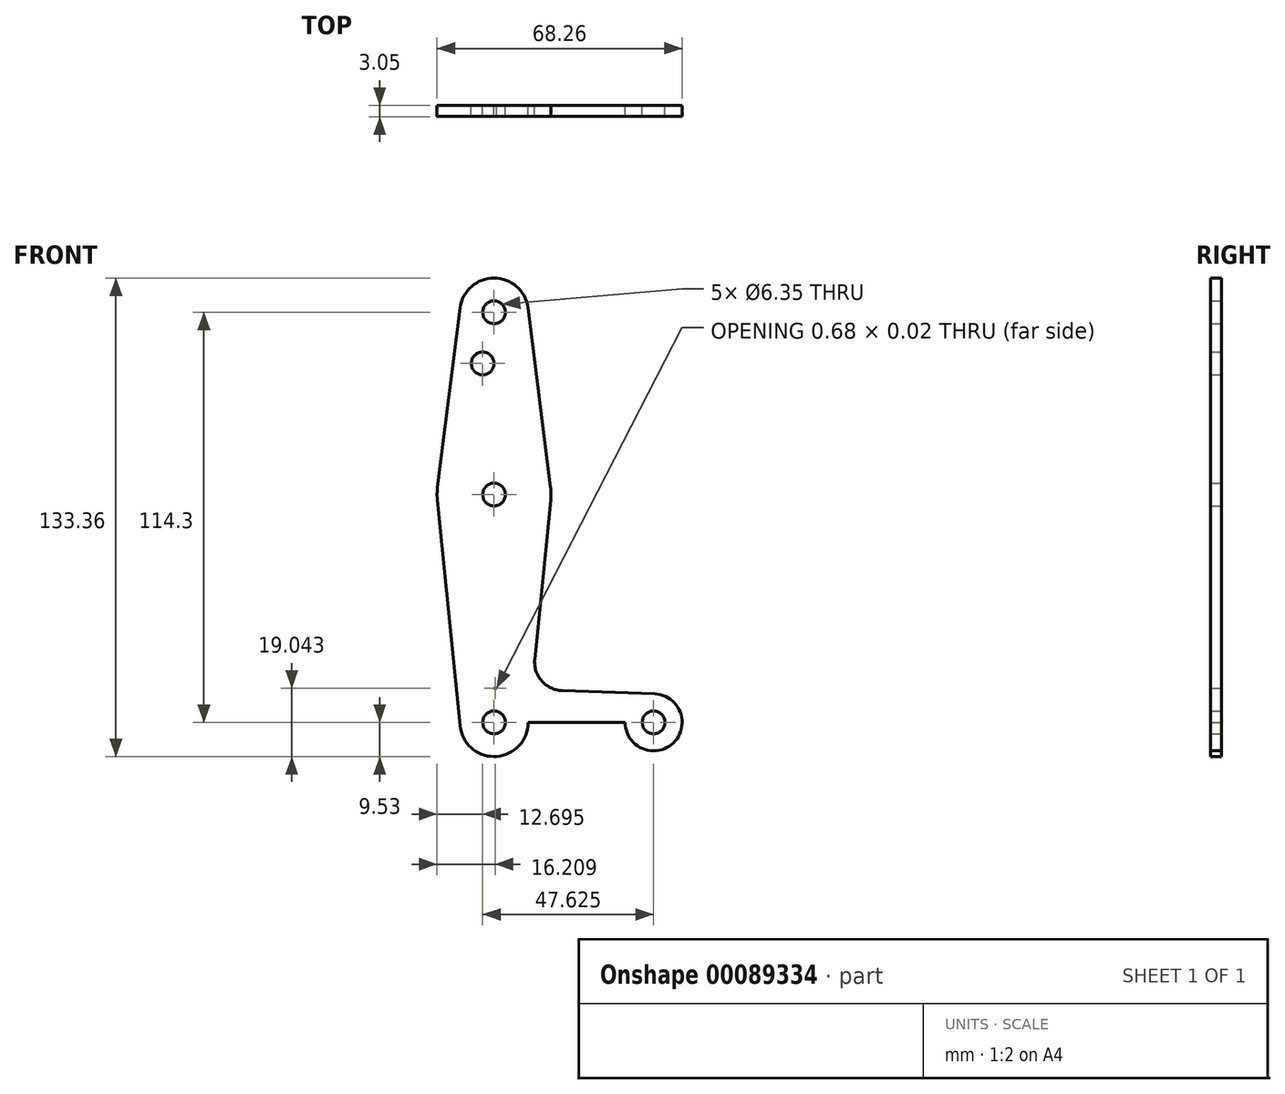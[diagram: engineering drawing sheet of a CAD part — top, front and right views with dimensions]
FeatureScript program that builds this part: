
annotation { "Feature Type Name" : "Feature", "Feature Type Description" : "" }
export const myFeature = defineFeature(function(context is Context, id is Id, definition is map)
    precondition{}
    {
        {
            var Q0;
            Q0=qCreatedBy(makeId("Front.planeOp"),FACE);
            var sketch = newSketch(context, id + "F0", { "sketchPlane" : qUnion([Q0])});
            skCircle(sketch, "E0", {"center": v(0, 114.3) * mm, "radius": 9.53 * mm});
            skCircle(sketch, "E1", {"center": v(0, 63.5) * mm, "radius": 15.88 * mm});
            skCircle(sketch, "E2", {"center": v(0, 0) * mm, "radius": 9.53 * mm});
            skCircle(sketch, "E3", {"center": v(44.45, 0) * mm, "radius": 7.94 * mm});
            skLineSegment(sketch, "E4", {"start": v(0, 114.3) * mm, "end": v(0, 0) * mm});
            skLineSegment(sketch, "E5", {"start": v(0, 0) * mm, "end": v(44.45, 0) * mm});
            skLineSegment(sketch, "E6", {"start": v(-9.45, 115.5) * mm, "end": v(-15.75, 65.48) * mm});
            skLineSegment(sketch, "E7", {"start": v(9.45, 115.5) * mm, "end": v(15.75, 65.48) * mm});
            skLineSegment(sketch, "E8", {"start": v(15.8, 61.91) * mm, "end": v(11.34, 17.59) * mm});
            skLineSegment(sketch, "E9", {"start": v(44.73, 7.93) * mm, "end": v(18.97, 8.85) * mm});
            skPoint(sketch, "E9.endSnap0", {"position": v(0, 57.15) * mm});
            skLineSegment(sketch, "E10", {"start": v(-15.8, 61.91) * mm, "end": v(-9.48, -0.95) * mm});
            skLineSegment(sketch, "E11", {"start": v(0, -9.52) * mm, "end": v(44.73, -7.93) * mm});
            skCircle(sketch, "E12", {"center": v(0, 114.3) * mm, "radius": 3.18 * mm});
            skCircle(sketch, "E13", {"center": v(-3.17, 100.03) * mm, "radius": 3.18 * mm});
            skCircle(sketch, "E14", {"center": v(0, 63.5) * mm, "radius": 3.18 * mm});
            skCircle(sketch, "E15", {"center": v(0, 0) * mm, "radius": 3.18 * mm});
            skCircle(sketch, "E16", {"center": v(44.45, 0) * mm, "radius": 3.18 * mm});
            skArc(sketch, "E17", {"start": v(11.34, 17.59) * mm, "mid": v(13.26, 11.57) * mm, "end": v(18.97, 8.85) * mm});
            skLineSegment(sketch, "E18.trimOffspring", {"start": v(0.68, 9.5) * mm, "end": v(0, 9.52) * mm});
            skSolve(sketch);
        }
        {
            var Q0;
            {var subQ5=sQuery(id+"F0.wireOp",EDGE,"E6");Q0=makeQuery(id+"F0.imprint","IMPRINT",FACE,{"disambiguationData":[TD([[makeQuery(id+"F0.imprint","IMPRINT",EDGE,{"derivedFrom":subQ5}),1.0]])]});}
            var Q1;
            {var subQ6=sQuery(id+"F0.wireOp",EDGE,"E7");Q1=makeQuery(id+"F0.imprint","IMPRINT",FACE,{"disambiguationData":[TD([[makeQuery(id+"F0.imprint","IMPRINT",EDGE,{"derivedFrom":subQ6}),-1.0]])]});}
            var Q2;
            {var subQ12=sQuery(id+"F0.wireOp",EDGE,"E8");Q2=makeQuery(id+"F0.imprint","IMPRINT",FACE,{"disambiguationData":[TD([[makeQuery(id+"F0.imprint","IMPRINT",EDGE,{"derivedFrom":subQ12}),-1.0]])]});}
            var Q3;
            {var subQ0=sQuery(id+"F0.wireOp",EDGE,"E10");Q3=makeQuery(id+"F0.imprint","IMPRINT",FACE,{"disambiguationData":[TD([[makeQuery(id+"F0.imprint","IMPRINT",EDGE,{"derivedFrom":subQ0}),1.0]])]});}
            var Q4;
            {var subQ0=sQuery(id+"F0.wireOp",EDGE,"E1");var subQ1=makeQuery(id+"F0.imprint","INTERSECT",VERTEX,{"derivedFrom":[subQ0,sQuery(id+"F0.wireOp",EDGE,"E7")]});Q4=makeQuery(id+"F0.imprint","IMPRINT",FACE,{"disambiguationData":[TD([[makeQuery(id+"F0.imprint","IMPRINT",EDGE,{"disambiguationData":[TD([[subQ1,-1.0]])],"derivedFrom":subQ0}),1.0]])]});}
            var Q5;
            {var subQ1=sQuery(id+"F0.wireOp",EDGE,"E1");var subQ8=makeQuery(id+"F0.imprint","INTERSECT",VERTEX,{"derivedFrom":[subQ1,sQuery(id+"F0.wireOp",EDGE,"E6")]});Q5=makeQuery(id+"F0.imprint","IMPRINT",FACE,{"disambiguationData":[TD([[makeQuery(id+"F0.imprint","IMPRINT",EDGE,{"disambiguationData":[TD([[subQ8,1.0]])],"derivedFrom":subQ1}),1.0]])]});}
            var Q6;
            Q6=makeQuery(id+"F0.imprint","IMPRINT",FACE,{"disambiguationData":[TD([[makeQuery(id+"F0.imprint","IMPRINT",EDGE,{"derivedFrom":sQuery(id+"F0.wireOp",EDGE,"E12")}),-1.0]])]});
            var Q7;
            {var subQ1=sQuery(id+"F0.wireOp",EDGE,"E2");var subQ5=makeQuery(id+"F0.imprint","INTERSECT",VERTEX,{"derivedFrom":[subQ1,sQuery(id+"F0.wireOp",EDGE,"E10")]});Q7=makeQuery(id+"F0.imprint","IMPRINT",FACE,{"disambiguationData":[TD([[makeQuery(id+"F0.imprint","IMPRINT",EDGE,{"disambiguationData":[TD([[subQ5,-1.0]])],"derivedFrom":subQ1}),1.0]])]});}
            var Q8;
            {var subQ7=sQuery(id+"F0.wireOp",EDGE,"E18.trimOffspring");Q8=makeQuery(id+"F0.imprint","IMPRINT",FACE,{"disambiguationData":[TD([[makeQuery(id+"F0.imprint","IMPRINT",EDGE,{"derivedFrom":subQ7}),1.0]])]});}
            var Q9;
            {var subQ0=sQuery(id+"F0.wireOp",EDGE,"E11");var subQ1=sQuery(id+"F0.wireOp",EDGE,"E2");var subQ2=makeQuery(id+"F0.imprint","INTERSECT",VERTEX,{"disambiguationData":[OD(1.0)],"derivedFrom":[subQ1,subQ0]});Q9=makeQuery(id+"F0.imprint","IMPRINT",FACE,{"disambiguationData":[TD([[makeQuery(id+"F0.imprint","IMPRINT",EDGE,{"disambiguationData":[TD([[subQ2,-1.0]])],"derivedFrom":subQ1}),-1.0]])]});}
            var Q10;
            Q10=makeQuery(id+"F0.imprint","IMPRINT",FACE,{"disambiguationData":[TD([[makeQuery(id+"F0.imprint","IMPRINT",EDGE,{"derivedFrom":sQuery(id+"F0.wireOp",EDGE,"E16")}),-1.0]])]});
            extrude(context, id + "F1", {"entities" : qUnion([Q0, Q1, Q2, Q3, Q4, Q5, Q6, Q7, Q8, Q9, Q10]), "depth" : 3.05 * mm});
        }
    });
